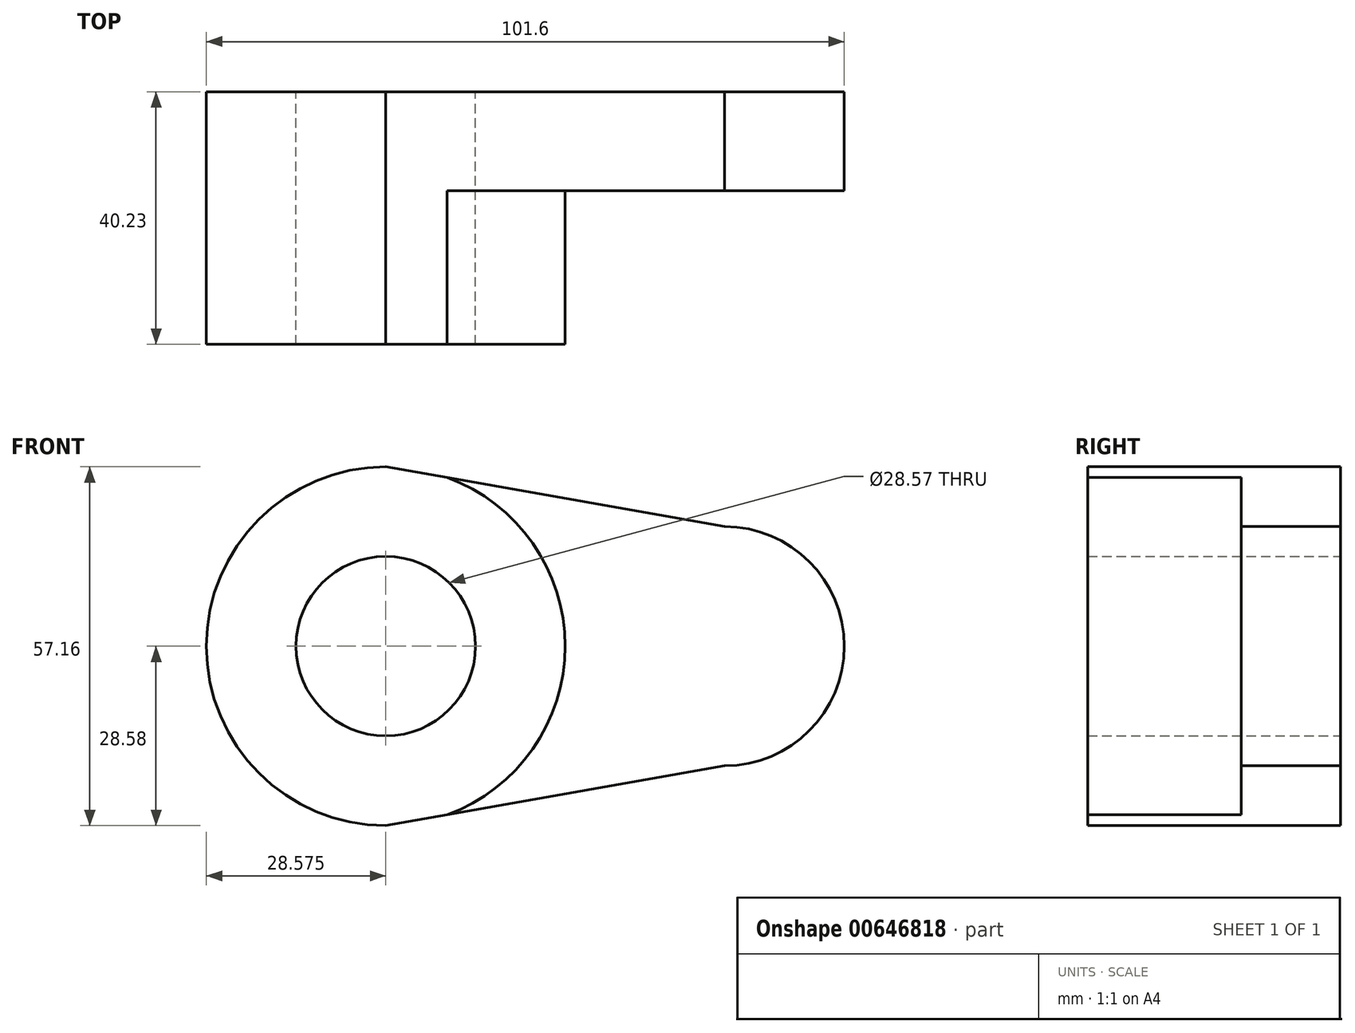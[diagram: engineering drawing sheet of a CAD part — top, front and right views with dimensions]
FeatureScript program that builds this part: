
annotation { "Feature Type Name" : "Feature", "Feature Type Description" : "" }
export const myFeature = defineFeature(function(context is Context, id is Id, definition is map)
    precondition{}
    {
        {
            var Q0;
            Q0=qCreatedBy(makeId("Front.planeOp"),FACE);
            var sketch = newSketch(context, id + "F0", { "sketchPlane" : qUnion([Q0])});
            skCircle(sketch, "E0", {"center": v(0, 0) * mm, "radius": 10.16 * mm});
            skLineSegment(sketch, "E1", {"start": v(0, 0) * mm, "end": v(-53.98, 0) * mm});
            skCircle(sketch, "E2", {"center": v(-53.98, 0) * mm, "radius": 14.29 * mm});
            skCircle(sketch, "E3", {"center": v(-53.98, 0) * mm, "radius": 28.58 * mm});
            skCircle(sketch, "E4", {"center": v(0, 0) * mm, "radius": 19.05 * mm});
            skLineSegment(sketch, "E5", {"start": v(0, 19.05) * mm, "end": v(-53.98, 28.58) * mm});
            skLineSegment(sketch, "E6", {"start": v(0, -19.05) * mm, "end": v(-53.98, -28.58) * mm});
            skSolve(sketch);
        }
        {
            var Q0;
            Q0=makeQuery(id+"F0.imprint","IMPRINT",FACE,{"disambiguationData":[TD([[makeQuery(id+"F0.imprint","IMPRINT",EDGE,{"derivedFrom":sQuery(id+"F0.wireOp",EDGE,"E2")}),-1.0]])]});
            extrude(context, id + "F1", {"entities" : qUnion([Q0]), "depth" : 40.23 * mm, "offsetDistance" : 25.4 * mm});
        }
        {
            var Q0;
            {var subQ0=sQuery(id+"F0.wireOp",EDGE,"E3");var subQ1=sQuery(id+"F0.wireOp",EDGE,"E1");var subQ2=makeQuery(id+"F0.imprint","INTERSECT",VERTEX,{"derivedFrom":[subQ1,subQ0]});Q0=makeQuery(id+"F0.imprint","IMPRINT",FACE,{"disambiguationData":[TD([[makeQuery(id+"F0.imprint","IMPRINT",EDGE,{"disambiguationData":[TD([[subQ2,1.0]])],"derivedFrom":subQ1}),-1.0]])]});}
            var Q1;
            {var subQ0=sQuery(id+"F0.wireOp",EDGE,"E3");var subQ1=sQuery(id+"F0.wireOp",EDGE,"E1");var subQ2=makeQuery(id+"F0.imprint","INTERSECT",VERTEX,{"derivedFrom":[subQ1,subQ0]});Q1=makeQuery(id+"F0.imprint","IMPRINT",FACE,{"disambiguationData":[TD([[makeQuery(id+"F0.imprint","IMPRINT",EDGE,{"disambiguationData":[TD([[subQ2,1.0]])],"derivedFrom":subQ1}),1.0]])]});}
            var Q2;
            Q2=makeQuery(id+"F0.imprint","IMPRINT",FACE,{"disambiguationData":[TD([[makeQuery(id+"F0.imprint","IMPRINT",EDGE,{"derivedFrom":sQuery(id+"F0.wireOp",EDGE,"E0")}),1.0]])]});
            var Q3;
            Q3=makeQuery(id+"F0.imprint","IMPRINT",FACE,{"disambiguationData":[TD([[makeQuery(id+"F0.imprint","IMPRINT",EDGE,{"derivedFrom":sQuery(id+"F0.wireOp",EDGE,"E0")}),-1.0]])]});
            extrude(context, id + "F2", {"entities" : qUnion([Q0, Q1, Q2, Q3]), "operationType" : NewBodyOperationType.ADD, "depth" : 15.77 * mm, "offsetDistance" : 25.4 * mm});
        }
    });
